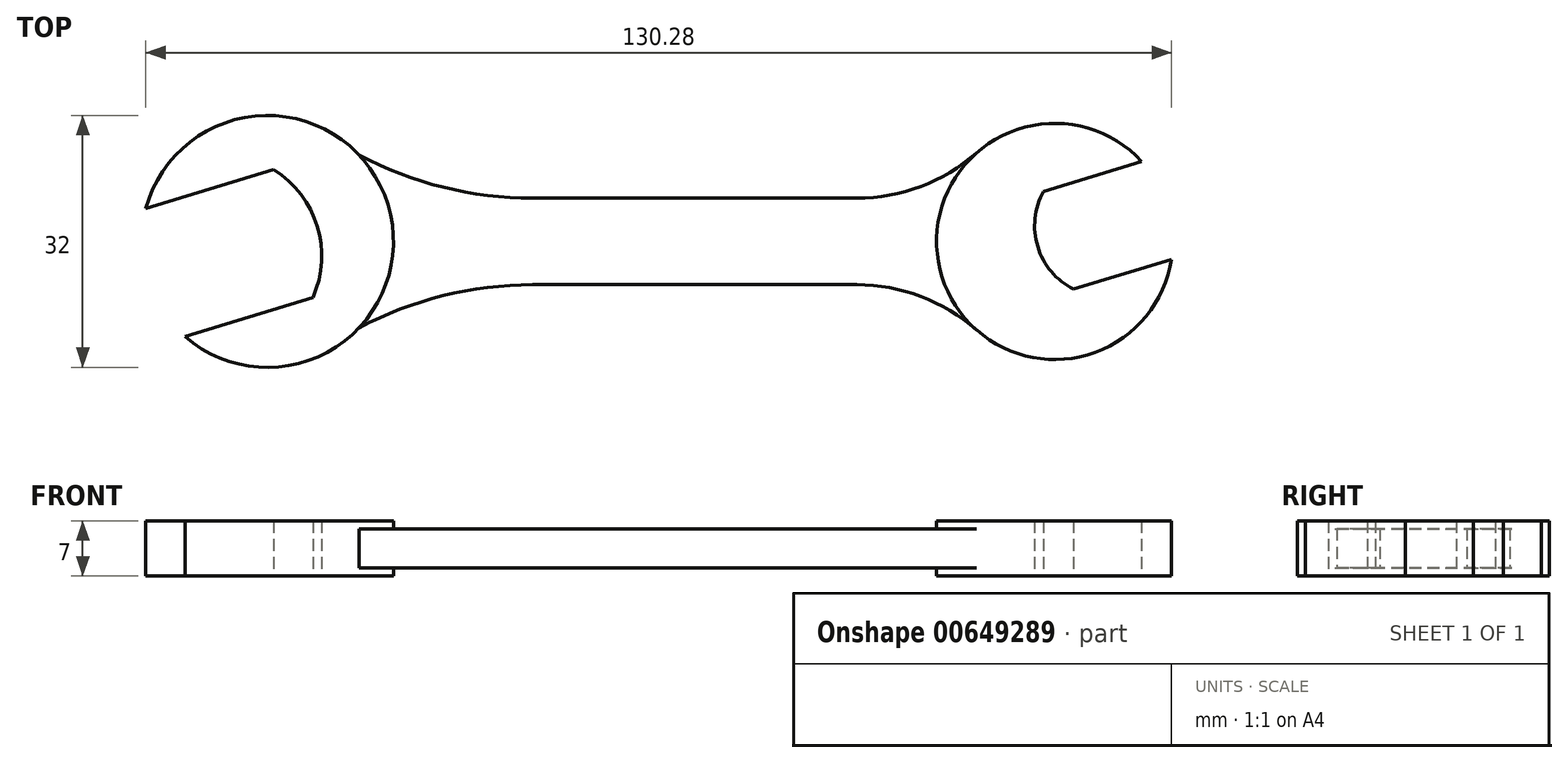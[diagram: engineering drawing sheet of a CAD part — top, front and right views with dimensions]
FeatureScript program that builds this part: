
annotation { "Feature Type Name" : "Feature", "Feature Type Description" : "" }
export const myFeature = defineFeature(function(context is Context, id is Id, definition is map)
    precondition{}
    {
        {
            var Q0;
            Q0=qCreatedBy(makeId("Top.planeOp"),FACE);
            var sketch = newSketch(context, id + "F0", { "sketchPlane" : qUnion([Q0])});
            skCircle(sketch, "E0", {"center": v(-50, 0) * mm, "radius": 16 * mm});
            skCircle(sketch, "E1", {"center": v(50, 0) * mm, "radius": 15 * mm});
            skPoint(sketch, "E2.middle", {"position": v(0, 0) * mm});
            skLineSegment(sketch, "E3.bottom", {"start": v(24.87, 5.5) * mm, "end": v(-16.33, 5.5) * mm});
            skLineSegment(sketch, "E3.top", {"start": v(24.87, -5.5) * mm, "end": v(-16.33, -5.5) * mm});
            skLineSegment(sketch, "E3.left", {"start": v(24.87, 5.5) * mm, "end": v(24.87, -5.5) * mm});
            skLineSegment(sketch, "E3.right", {"start": v(-16.33, 5.5) * mm, "end": v(-16.33, -5.5) * mm});
            skArc(sketch, "E4", {"start": v(-38.36, 10.98) * mm, "mid": v(-27.69, 6.9) * mm, "end": v(-16.33, 5.5) * mm});
            skArc(sketch, "E5", {"start": v(-16.33, -5.5) * mm, "mid": v(-27.69, -6.9) * mm, "end": v(-38.36, -10.98) * mm});
            skArc(sketch, "E6", {"start": v(40.1, -11.26) * mm, "mid": v(33, -6.99) * mm, "end": v(24.87, -5.5) * mm});
            skArc(sketch, "E7", {"start": v(24.87, 5.5) * mm, "mid": v(32.99, 6.98) * mm, "end": v(40.06, 11.24) * mm});
            skLineSegment(sketch, "E8", {"start": v(-60.48, -12.1) * mm, "end": v(-44.22, -7.12) * mm});
            skLineSegment(sketch, "E9", {"start": v(-49.2, 9.14) * mm, "end": v(-65.45, 4.17) * mm});
            skArc(sketch, "E10", {"start": v(-44.22, -7.12) * mm, "mid": v(-43.68, 1.93) * mm, "end": v(-49.2, 9.14) * mm});
            skLineSegment(sketch, "E11", {"start": v(61.03, 10.17) * mm, "end": v(48.6, 6.37) * mm});
            skLineSegment(sketch, "E12", {"start": v(52.4, -6.06) * mm, "end": v(64.83, -2.26) * mm});
            skArc(sketch, "E13", {"start": v(48.6, 6.37) * mm, "mid": v(47.84, -0.66) * mm, "end": v(52.4, -6.06) * mm});
            skSolve(sketch);
        }
        {
            var Q0;
            Q0=makeQuery(id+"F0.imprint","IMPRINT",FACE,{"disambiguationData":[TD([[makeQuery(id+"F0.imprint","IMPRINT",EDGE,{"derivedFrom":sQuery(id+"F0.wireOp",EDGE,"E3.right")}),-1.0]])]});
            var Q1;
            Q1=makeQuery(id+"F0.imprint","IMPRINT",FACE,{"disambiguationData":[TD([[makeQuery(id+"F0.imprint","IMPRINT",EDGE,{"derivedFrom":sQuery(id+"F0.wireOp",EDGE,"E3.bottom")}),1.0]])]});
            var Q2;
            Q2=makeQuery(id+"F0.imprint","IMPRINT",FACE,{"disambiguationData":[TD([[makeQuery(id+"F0.imprint","IMPRINT",EDGE,{"derivedFrom":sQuery(id+"F0.wireOp",EDGE,"E3.left")}),1.0]])]});
            extrude(context, id + "F1", {"entities" : qUnion([Q0, Q1, Q2]), "endBound" : BoundingType.SYMMETRIC, "depth" : 5 * mm, "offsetDistance" : 25 * mm});
        }
        {
            var Q0;
            {var subQ0=sQuery(id+"F0.wireOp",EDGE,"E8");Q0=makeQuery(id+"F0.imprint","IMPRINT",FACE,{"disambiguationData":[TD([[makeQuery(id+"F0.imprint","IMPRINT",EDGE,{"derivedFrom":subQ0}),-1.0]])]});}
            var Q1;
            {var subQ4=sQuery(id+"F0.wireOp",EDGE,"E11");Q1=makeQuery(id+"F0.imprint","IMPRINT",FACE,{"disambiguationData":[TD([[makeQuery(id+"F0.imprint","IMPRINT",EDGE,{"derivedFrom":subQ4}),-1.0]])]});}
            extrude(context, id + "F2", {"entities" : qUnion([Q0, Q1]), "operationType" : NewBodyOperationType.ADD, "endBound" : BoundingType.SYMMETRIC, "depth" : 7 * mm, "offsetDistance" : 25 * mm});
        }
    });
